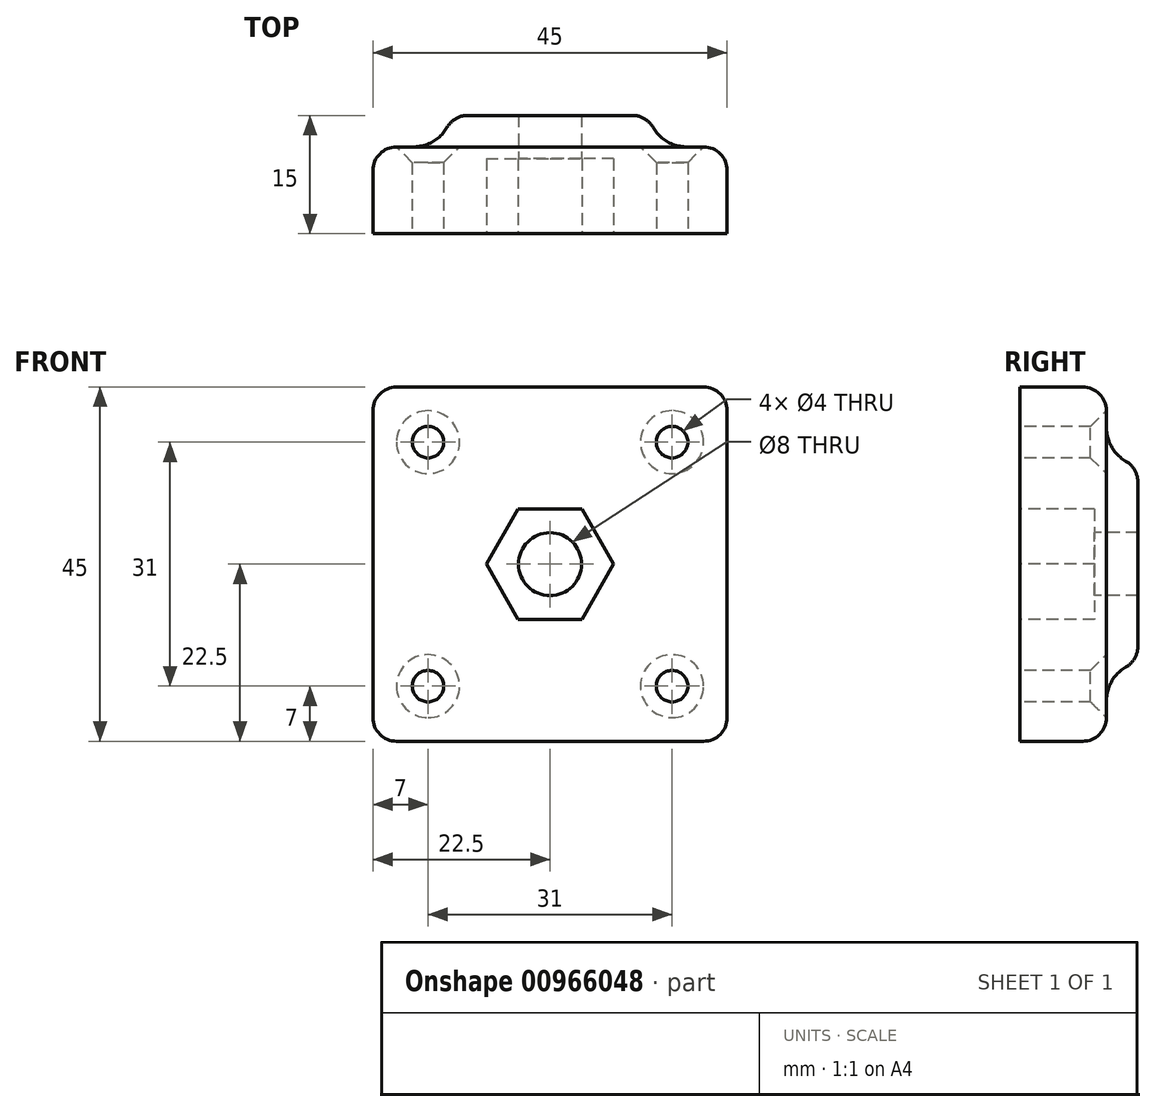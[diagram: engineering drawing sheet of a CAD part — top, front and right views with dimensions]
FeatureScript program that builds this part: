
annotation { "Feature Type Name" : "Feature", "Feature Type Description" : "" }
export const myFeature = defineFeature(function(context is Context, id is Id, definition is map)
    precondition{}
    {
        {
            var Q0;
            Q0=qCreatedBy(makeId("Front.planeOp"),FACE);
            var sketch = newSketch(context, id + "F0", { "sketchPlane" : qUnion([Q0])});
            skLineSegment(sketch, "E0.bottom", {"start": v(22.5, -22.5) * mm, "end": v(-22.5, -22.5) * mm});
            skLineSegment(sketch, "E0.top", {"start": v(22.5, 22.5) * mm, "end": v(-22.5, 22.5) * mm});
            skLineSegment(sketch, "E0.left", {"start": v(22.5, -22.5) * mm, "end": v(22.5, 22.5) * mm});
            skLineSegment(sketch, "E0.right", {"start": v(-22.5, -22.5) * mm, "end": v(-22.5, 22.5) * mm});
            skPoint(sketch, "E0.middle", {"position": v(0, 0) * mm});
            skCircle(sketch, "E1", {"center": v(0, 0) * mm, "radius": 12.5 * mm});
            skCircle(sketch, "E2", {"center": v(0, 0) * mm, "radius": 4 * mm});
            skCircle(sketch, "E3.cCircle", {"center": v(0, 0) * mm, "radius": 7 * mm, "construction": true});
            skLineSegment(sketch, "E3.0", {"start": v(4.04, -7) * mm, "end": v(-4.04, -7) * mm});
            skLineSegment(sketch, "E3.1", {"start": v(-4.04, -7) * mm, "end": v(-8.08, 0) * mm});
            skLineSegment(sketch, "E3.2", {"start": v(-8.08, 0) * mm, "end": v(-4.04, 7) * mm});
            skLineSegment(sketch, "E3.3", {"start": v(-4.04, 7) * mm, "end": v(4.04, 7) * mm});
            skLineSegment(sketch, "E3.4", {"start": v(4.04, 7) * mm, "end": v(8.08, 0) * mm});
            skLineSegment(sketch, "E3.5", {"start": v(8.08, 0) * mm, "end": v(4.04, -7) * mm});
            skPoint(sketch, "E3.0.midPoint", {"position": v(0, -7) * mm});
            skLineSegment(sketch, "E4.bottom", {"start": v(22.5, -22.5) * mm, "end": v(15.5, -22.5) * mm});
            skLineSegment(sketch, "E4.top", {"start": v(22.5, -15.5) * mm, "end": v(15.5, -15.5) * mm});
            skLineSegment(sketch, "E4.left", {"start": v(22.5, -22.5) * mm, "end": v(22.5, -15.5) * mm});
            skLineSegment(sketch, "E4.right", {"start": v(15.5, -22.5) * mm, "end": v(15.5, -15.5) * mm});
            skCircle(sketch, "E5", {"center": v(15.5, -15.5) * mm, "radius": 2 * mm});
            skLineSegment(sketch, "E6.bottom", {"start": v(22.5, 22.5) * mm, "end": v(15.5, 22.5) * mm});
            skLineSegment(sketch, "E6.top", {"start": v(22.5, 15.5) * mm, "end": v(15.5, 15.5) * mm});
            skLineSegment(sketch, "E6.left", {"start": v(22.5, 22.5) * mm, "end": v(22.5, 15.5) * mm});
            skLineSegment(sketch, "E6.right", {"start": v(15.5, 22.5) * mm, "end": v(15.5, 15.5) * mm});
            skLineSegment(sketch, "E7.bottom", {"start": v(-22.5, 22.5) * mm, "end": v(-15.5, 22.5) * mm});
            skLineSegment(sketch, "E7.top", {"start": v(-22.5, 15.5) * mm, "end": v(-15.5, 15.5) * mm});
            skLineSegment(sketch, "E7.left", {"start": v(-22.5, 22.5) * mm, "end": v(-22.5, 15.5) * mm});
            skLineSegment(sketch, "E7.right", {"start": v(-15.5, 22.5) * mm, "end": v(-15.5, 15.5) * mm});
            skLineSegment(sketch, "E8.bottom", {"start": v(-22.5, -22.5) * mm, "end": v(-15.5, -22.5) * mm});
            skLineSegment(sketch, "E8.top", {"start": v(-22.5, -15.5) * mm, "end": v(-15.5, -15.5) * mm});
            skLineSegment(sketch, "E8.left", {"start": v(-22.5, -22.5) * mm, "end": v(-22.5, -15.5) * mm});
            skLineSegment(sketch, "E8.right", {"start": v(-15.5, -22.5) * mm, "end": v(-15.5, -15.5) * mm});
            skCircle(sketch, "E9", {"center": v(15.5, 15.5) * mm, "radius": 2 * mm});
            skCircle(sketch, "E10", {"center": v(-15.5, 15.5) * mm, "radius": 2 * mm});
            skCircle(sketch, "E11", {"center": v(-15.5, -15.5) * mm, "radius": 2 * mm});
            skSolve(sketch);
        }
        {
            var Q0;
            Q0=makeQuery(id+"F0.imprint","IMPRINT",FACE,{"disambiguationData":[TD([[makeQuery(id+"F0.imprint","IMPRINT",EDGE,{"derivedFrom":sQuery(id+"F0.wireOp",EDGE,"E1")}),1.0]])]});
            var Q1;
            Q1=makeQuery(id+"F0.imprint","IMPRINT",FACE,{"disambiguationData":[TD([[makeQuery(id+"F0.imprint","IMPRINT",EDGE,{"derivedFrom":sQuery(id+"F0.wireOp",EDGE,"E2")}),-1.0]])]});
            var Q2;
            {var subQ1=sQuery(id+"F0.wireOp",EDGE,"E0.top");Q2=makeQuery(id+"F0.imprint","IMPRINT",FACE,{"disambiguationData":[TD([[makeQuery(id+"F0.imprint","IMPRINT",EDGE,{"derivedFrom":subQ1}),1.0]])]});}
            var Q3;
            {var subQ5=sQuery(id+"F0.wireOp",EDGE,"E0.bottom");var subQ7=sQuery(id+"F0.wireOp",EDGE,"E4.right");var subQ8=makeQuery(id+"F0.imprint","INTERSECT",VERTEX,{"derivedFrom":[subQ5,subQ7]});Q3=makeQuery(id+"F0.imprint","IMPRINT",FACE,{"disambiguationData":[TD([[makeQuery(id+"F0.imprint","IMPRINT",EDGE,{"disambiguationData":[TD([[subQ8,1.0]])],"derivedFrom":subQ5}),-1.0]])]});}
            var Q4;
            Q4=makeQuery(id+"F0.imprint","IMPRINT",FACE,{"disambiguationData":[TD([[makeQuery(id+"F0.imprint","IMPRINT",EDGE,{"derivedFrom":sQuery(id+"F0.wireOp",EDGE,"E1")}),-1.0]])]});
            var Q5;
            {var subQ1=sQuery(id+"F0.wireOp",EDGE,"E0.bottom");var subQ6=sQuery(id+"F0.wireOp",EDGE,"E0.right");var subQ9=makeQuery(id+"F0.imprint","INTERSECT",VERTEX,{"derivedFrom":[subQ1,subQ6]});Q5=makeQuery(id+"F0.imprint","IMPRINT",FACE,{"disambiguationData":[TD([[makeQuery(id+"F0.imprint","IMPRINT",EDGE,{"disambiguationData":[TD([[subQ9,1.0]])],"derivedFrom":subQ1}),-1.0]])]});}
            extrude(context, id + "F1", {"entities" : qUnion([Q0, Q1, Q2, Q3, Q4, Q5]), "oppositeDirection" : true, "depth" : 11 * mm, "offsetDistance" : 25 * mm});
        }
        {
            var Q0;
            Q0=makeQuery(id+"F0.imprint","IMPRINT",FACE,{"disambiguationData":[TD([[makeQuery(id+"F0.imprint","IMPRINT",EDGE,{"derivedFrom":sQuery(id+"F0.wireOp",EDGE,"E1")}),1.0]])]});
            var Q1;
            Q1=makeQuery(id+"F0.imprint","IMPRINT",FACE,{"disambiguationData":[TD([[makeQuery(id+"F0.imprint","IMPRINT",EDGE,{"derivedFrom":sQuery(id+"F0.wireOp",EDGE,"E2")}),-1.0]])]});
            extrude(context, id + "F2", {"entities" : qUnion([Q0, Q1]), "operationType" : NewBodyOperationType.ADD, "oppositeDirection" : true, "depth" : 15 * mm, "offsetDistance" : 25 * mm});
        }
        {
            var Q0;
            Q0=makeQuery(id+"F0.imprint","IMPRINT",FACE,{"disambiguationData":[TD([[makeQuery(id+"F0.imprint","IMPRINT",EDGE,{"derivedFrom":sQuery(id+"F0.wireOp",EDGE,"E2")}),-1.0]])]});
            extrude(context, id + "F3", {"entities" : qUnion([Q0]), "operationType" : NewBodyOperationType.REMOVE, "oppositeDirection" : true, "depth" : 9.5 * mm, "offsetDistance" : 25 * mm});
        }
        {
            var Q0;
            Q0=makeQuery(id+"F2.boolean.opBoolean","INTERSECT",EDGE,{"derivedFrom":[makeQuery(id+"F1.opExtrude","CAP_FACE",FACE,{"disambiguationData":[OSD([sQuery(id+"F0.wireOp",EDGE,"E0.bottom"),sQuery(id+"F0.wireOp",EDGE,"E0.top"),sQuery(id+"F0.wireOp",EDGE,"E0.left"),sQuery(id+"F0.wireOp",EDGE,"E0.right"),sQuery(id+"F0.wireOp",EDGE,"E2"),sQuery(id+"F0.wireOp",EDGE,"E5"),sQuery(id+"F0.wireOp",EDGE,"E9"),sQuery(id+"F0.wireOp",EDGE,"E10"),sQuery(id+"F0.wireOp",EDGE,"E11")])],"isStart":false}),makeQuery(id+"F2.opExtrude","SWEPT_FACE",FACE,{"disambiguationData":[OSD([sQuery(id+"F0.wireOp",EDGE,"E1")])]})]});
            fillet(context, id + "F4", {"entities" : qUnion([Q0]), "tangentPropagation" : true, "radius" : 5 * mm, "defaultsChanged" : false, "vertexSettings" : [], "allowEdgeOverflow" : false});
        }
        {
            var Q0;
            {var subQ0=sQuery(id+"F0.wireOp",EDGE,"E2");var subQ1=sQuery(id+"F0.wireOp",EDGE,"E1");Q0=makeQuery(id+"F4.opFillet","BLEND_EDGE",EDGE,{"blendedFrom":[makeQuery(id+"F2.boolean.opBoolean","INTERSECT",EDGE,{"derivedFrom":[makeQuery(id+"F1.opExtrude","CAP_FACE",FACE,{"disambiguationData":[OSD([sQuery(id+"F0.wireOp",EDGE,"E0.bottom"),sQuery(id+"F0.wireOp",EDGE,"E0.top"),sQuery(id+"F0.wireOp",EDGE,"E0.left"),sQuery(id+"F0.wireOp",EDGE,"E0.right"),subQ0,sQuery(id+"F0.wireOp",EDGE,"E5"),sQuery(id+"F0.wireOp",EDGE,"E9"),sQuery(id+"F0.wireOp",EDGE,"E10"),sQuery(id+"F0.wireOp",EDGE,"E11")])],"isStart":false}),makeQuery(id+"F2.opExtrude","SWEPT_FACE",FACE,{"disambiguationData":[OSD([subQ1])]})]}),makeQuery(id+"F2.opExtrude","CAP_FACE",FACE,{"disambiguationData":[OSD([subQ1,subQ0])],"isStart":false})],"blendedInto":[makeQuery(id+"F2.opExtrude","CAP_FACE",FACE,{"disambiguationData":[OSD([subQ1,subQ0])],"isStart":false})]});}
            var Q1;
            Q1=makeQuery(id+"F1.opExtrude","CAP_EDGE",EDGE,{"disambiguationData":[OSD([sQuery(id+"F0.wireOp",EDGE,"E0.bottom")])],"isStart":false});
            var Q2;
            Q2=makeQuery(id+"F1.opExtrude","CAP_EDGE",EDGE,{"disambiguationData":[OSD([sQuery(id+"F0.wireOp",EDGE,"E0.right")])],"isStart":false});
            var Q3;
            Q3=makeQuery(id+"F1.opExtrude","SWEPT_EDGE",EDGE,{"disambiguationData":[OSD([sQuery(id+"F0.wireOp",EDGE,"E0.bottom"),sQuery(id+"F0.wireOp",EDGE,"E0.right")])]});
            var Q4;
            Q4=makeQuery(id+"F1.opExtrude","SWEPT_EDGE",EDGE,{"disambiguationData":[OSD([sQuery(id+"F0.wireOp",EDGE,"E0.top"),sQuery(id+"F0.wireOp",EDGE,"E0.right")])]});
            var Q5;
            Q5=makeQuery(id+"F1.opExtrude","CAP_EDGE",EDGE,{"disambiguationData":[OSD([sQuery(id+"F0.wireOp",EDGE,"E0.top")])],"isStart":false});
            var Q6;
            Q6=makeQuery(id+"F1.opExtrude","SWEPT_EDGE",EDGE,{"disambiguationData":[OSD([sQuery(id+"F0.wireOp",EDGE,"E0.top"),sQuery(id+"F0.wireOp",EDGE,"E0.left")])]});
            var Q7;
            Q7=makeQuery(id+"F1.opExtrude","CAP_EDGE",EDGE,{"disambiguationData":[OSD([sQuery(id+"F0.wireOp",EDGE,"E0.left")])],"isStart":false});
            var Q8;
            Q8=makeQuery(id+"F1.opExtrude","SWEPT_EDGE",EDGE,{"disambiguationData":[OSD([sQuery(id+"F0.wireOp",EDGE,"E0.bottom"),sQuery(id+"F0.wireOp",EDGE,"E0.left")])]});
            fillet(context, id + "F5", {"entities" : qUnion([Q0, Q1, Q2, Q3, Q4, Q5, Q6, Q7, Q8]), "tangentPropagation" : true, "radius" : 3 * mm, "defaultsChanged" : false, "vertexSettings" : [], "allowEdgeOverflow" : false});
        }
        {
            var Q0;
            Q0=makeQuery(id+"F1.opExtrude","CAP_EDGE",EDGE,{"disambiguationData":[OSD([sQuery(id+"F0.wireOp",EDGE,"E10")])],"isStart":false});
            var Q1;
            Q1=makeQuery(id+"F1.opExtrude","CAP_EDGE",EDGE,{"disambiguationData":[OSD([sQuery(id+"F0.wireOp",EDGE,"E11")])],"isStart":false});
            var Q2;
            Q2=makeQuery(id+"F1.opExtrude","CAP_EDGE",EDGE,{"disambiguationData":[OSD([sQuery(id+"F0.wireOp",EDGE,"E5")])],"isStart":false});
            var Q3;
            Q3=makeQuery(id+"F1.opExtrude","CAP_EDGE",EDGE,{"disambiguationData":[OSD([sQuery(id+"F0.wireOp",EDGE,"E9")])],"isStart":false});
            chamfer(context, id + "F6", {"entities" : qUnion([Q0, Q1, Q2, Q3]), "width" : 2 * mm, "tangentPropagation" : true});
        }
    });
